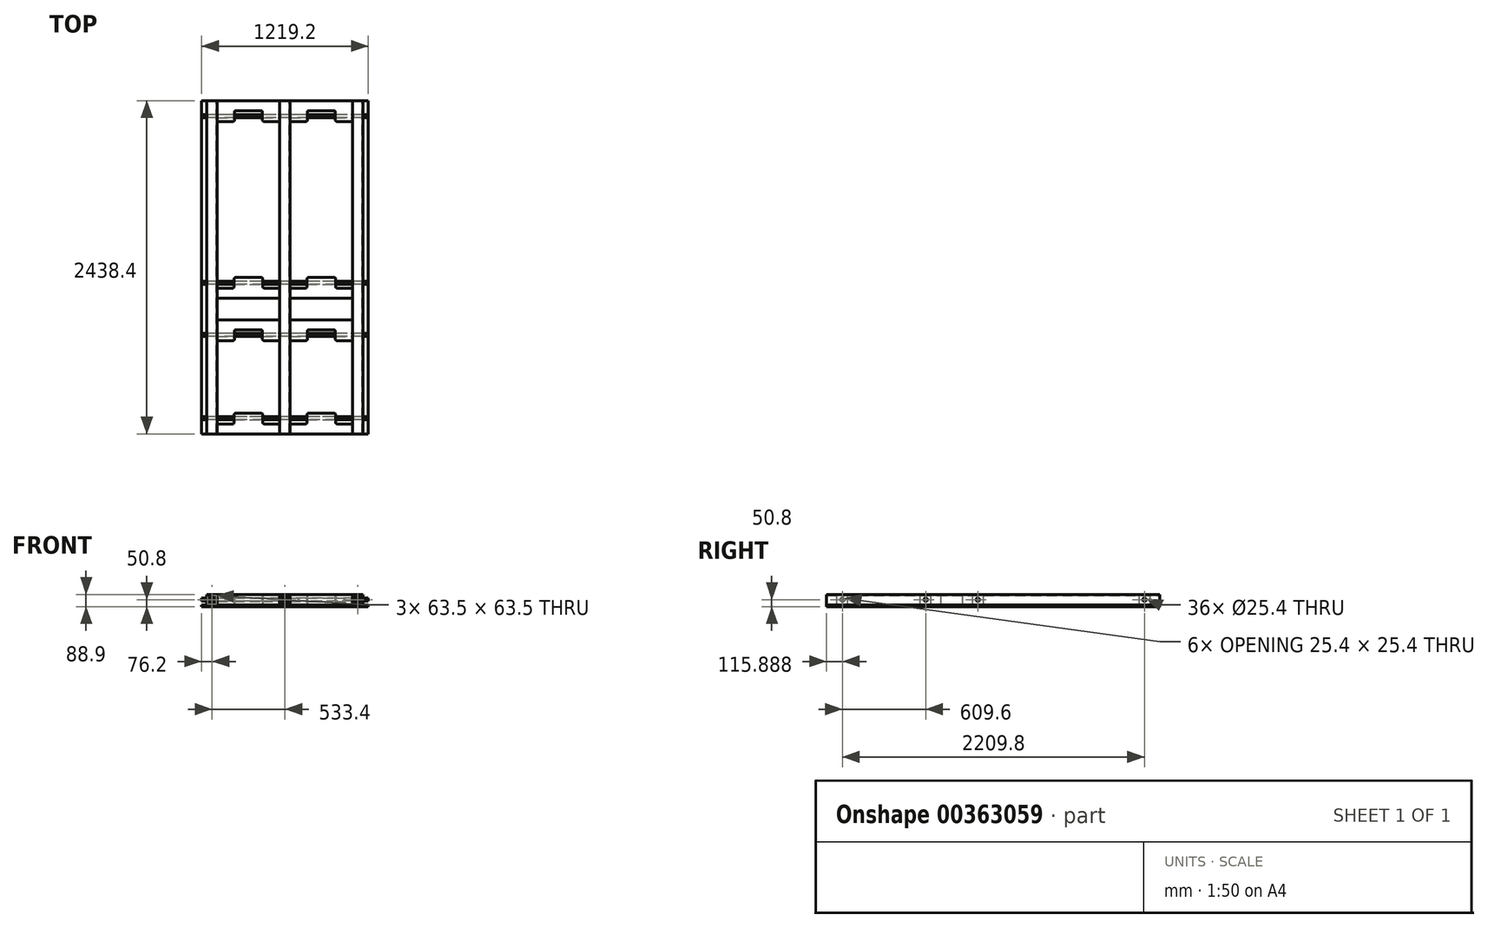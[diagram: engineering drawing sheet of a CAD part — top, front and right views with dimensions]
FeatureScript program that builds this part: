
annotation { "Feature Type Name" : "Feature", "Feature Type Description" : "" }
export const myFeature = defineFeature(function(context is Context, id is Id, definition is map)
    precondition{}
    {
        {
            var Q0;
            Q0=qCreatedBy(makeId("Top.planeOp"),FACE);
            var sketch = newSketch(context, id + "F0", { "sketchPlane" : qUnion([Q0])});
            skLineSegment(sketch, "E0.bottom", {"start": v(-609.6, 1219.2) * mm, "end": v(609.6, 1219.2) * mm});
            skLineSegment(sketch, "E0.top", {"start": v(-609.6, -1219.2) * mm, "end": v(609.6, -1219.2) * mm});
            skLineSegment(sketch, "E0.left", {"start": v(-609.6, 1219.2) * mm, "end": v(-609.6, -1219.2) * mm});
            skLineSegment(sketch, "E0.right", {"start": v(609.6, 1219.2) * mm, "end": v(609.6, -1219.2) * mm});
            skPoint(sketch, "E0.middle", {"position": v(0, 0) * mm});
            skSolve(sketch);
        }
        {
            var Q0;
            Q0 = qSketchRegion(id + "F0", true);
            extrude(context, id + "F1", {"entities" : qUnion([Q0]), "depth" : 12.7 * mm});
        }
        {
            var Q0;
            Q0=qCreatedBy(makeId("Front.planeOp"),FACE);
            var sketch = newSketch(context, id + "F2", { "sketchPlane" : qUnion([Q0])});
            skLineSegment(sketch, "E1.bottom", {"start": v(38.1, 88.9) * mm, "end": v(-38.1, 88.9) * mm});
            skLineSegment(sketch, "E1.top", {"start": v(38.1, 12.7) * mm, "end": v(-38.1, 12.7) * mm});
            skLineSegment(sketch, "E1.left", {"start": v(38.1, 88.9) * mm, "end": v(38.1, 12.7) * mm});
            skLineSegment(sketch, "E1.right", {"start": v(-38.1, 88.9) * mm, "end": v(-38.1, 12.7) * mm});
            skPoint(sketch, "E1.middle", {"position": v(0, 50.8) * mm});
            skLineSegment(sketch, "E2.bottom", {"start": v(31.75, 82.55) * mm, "end": v(-31.75, 82.55) * mm});
            skLineSegment(sketch, "E2.top", {"start": v(31.75, 19.05) * mm, "end": v(-31.75, 19.05) * mm});
            skLineSegment(sketch, "E2.left", {"start": v(31.75, 82.55) * mm, "end": v(31.75, 19.05) * mm});
            skLineSegment(sketch, "E2.right", {"start": v(-31.75, 82.55) * mm, "end": v(-31.75, 19.05) * mm});
            skLineSegment(sketch, "E3.bottom", {"start": v(-495.3, 88.9) * mm, "end": v(-571.5, 88.9) * mm});
            skLineSegment(sketch, "E3.top", {"start": v(-495.3, 12.7) * mm, "end": v(-571.5, 12.7) * mm});
            skLineSegment(sketch, "E3.left", {"start": v(-495.3, 88.9) * mm, "end": v(-495.3, 12.7) * mm});
            skLineSegment(sketch, "E3.right", {"start": v(-571.5, 88.9) * mm, "end": v(-571.5, 12.7) * mm});
            skPoint(sketch, "E3.middle", {"position": v(-533.4, 50.8) * mm});
            skLineSegment(sketch, "E4.bottom", {"start": v(571.5, 88.9) * mm, "end": v(495.3, 88.9) * mm});
            skLineSegment(sketch, "E4.top", {"start": v(571.5, 12.7) * mm, "end": v(495.3, 12.7) * mm});
            skLineSegment(sketch, "E4.left", {"start": v(571.5, 88.9) * mm, "end": v(571.5, 12.7) * mm});
            skLineSegment(sketch, "E4.right", {"start": v(495.3, 88.9) * mm, "end": v(495.3, 12.7) * mm});
            skPoint(sketch, "E4.middle", {"position": v(533.4, 50.8) * mm});
            skLineSegment(sketch, "E5.bottom", {"start": v(-565.15, 82.55) * mm, "end": v(-501.65, 82.55) * mm});
            skLineSegment(sketch, "E5.top", {"start": v(-565.15, 19.05) * mm, "end": v(-501.65, 19.05) * mm});
            skLineSegment(sketch, "E5.left", {"start": v(-565.15, 82.55) * mm, "end": v(-565.15, 19.05) * mm});
            skLineSegment(sketch, "E5.right", {"start": v(-501.65, 82.55) * mm, "end": v(-501.65, 19.05) * mm});
            skLineSegment(sketch, "E6.bottom", {"start": v(501.65, 82.55) * mm, "end": v(565.15, 82.55) * mm});
            skLineSegment(sketch, "E6.top", {"start": v(501.65, 19.05) * mm, "end": v(565.15, 19.05) * mm});
            skLineSegment(sketch, "E6.left", {"start": v(501.65, 82.55) * mm, "end": v(501.65, 19.05) * mm});
            skLineSegment(sketch, "E6.right", {"start": v(565.15, 82.55) * mm, "end": v(565.15, 19.05) * mm});
            skSolve(sketch);
        }
        {
            var Q0;
            Q0 = qSketchRegion(id + "F2", true);
            extrude(context, id + "F3", {"entities" : qUnion([Q0]), "endBound" : BoundingType.SYMMETRIC, "depth" : 2438.4 * mm});
        }
        {
            var Q0;
            Q0=makeQuery(id+"F1.opExtrude","CAP_FACE",FACE,{"disambiguationData":[OSD([sQuery(id+"F0.wireOp",EDGE,"E0.bottom"),sQuery(id+"F0.wireOp",EDGE,"E0.top"),sQuery(id+"F0.wireOp",EDGE,"E0.left"),sQuery(id+"F0.wireOp",EDGE,"E0.right")])],"isStart":false});
            var sketch = newSketch(context, id + "F4", { "sketchPlane" : qUnion([Q0])});
            skLineSegment(sketch, "E7", {"start": v(-495.3, 1219.2) * mm, "end": v(-495.3, 1066.8) * mm});
            skLineSegment(sketch, "E8", {"start": v(-495.3, 1066.8) * mm, "end": v(-368.3, 1066.8) * mm});
            skLineSegment(sketch, "E9", {"start": v(-368.3, 1066.8) * mm, "end": v(-368.3, 1146.18) * mm});
            skLineSegment(sketch, "E10", {"start": v(-368.3, 1146.17) * mm, "end": v(-165.1, 1146.17) * mm});
            skLineSegment(sketch, "E11", {"start": v(-165.1, 1146.18) * mm, "end": v(-165.1, 1066.8) * mm});
            skLineSegment(sketch, "E12", {"start": v(-165.1, 1066.8) * mm, "end": v(-38.1, 1066.8) * mm});
            skLineSegment(sketch, "E13", {"start": v(-38.1, 1066.8) * mm, "end": v(-38.1, 1219.2) * mm});
            skLineSegment(sketch, "E14", {"start": v(-38.1, 1219.2) * mm, "end": v(-495.3, 1219.2) * mm});
            skLineSegment(sketch, "E15", {"start": v(-495.3, -152.4) * mm, "end": v(-371.48, -152.4) * mm});
            skLineSegment(sketch, "E16", {"start": v(-371.48, -152.4) * mm, "end": v(-371.48, -73.03) * mm});
            skLineSegment(sketch, "E17", {"start": v(-371.48, -73.03) * mm, "end": v(-161.93, -73.03) * mm});
            skLineSegment(sketch, "E18", {"start": v(-161.93, -73.02) * mm, "end": v(-161.93, -152.4) * mm});
            skLineSegment(sketch, "E19", {"start": v(-161.93, -152.4) * mm, "end": v(-38.1, -152.4) * mm});
            skLineSegment(sketch, "E20", {"start": v(-38.1, -152.4) * mm, "end": v(-38.1, -536.57) * mm});
            skLineSegment(sketch, "E21", {"start": v(-38.1, -536.57) * mm, "end": v(-165.1, -536.57) * mm});
            skLineSegment(sketch, "E22", {"start": v(-165.1, -536.57) * mm, "end": v(-165.1, -457.2) * mm});
            skLineSegment(sketch, "E23", {"start": v(-165.1, -457.2) * mm, "end": v(-368.3, -457.2) * mm});
            skLineSegment(sketch, "E24", {"start": v(-368.3, -457.2) * mm, "end": v(-368.3, -536.57) * mm});
            skLineSegment(sketch, "E25", {"start": v(-368.3, -536.57) * mm, "end": v(-495.3, -536.57) * mm});
            skLineSegment(sketch, "E26", {"start": v(-495.3, -536.57) * mm, "end": v(-495.3, -152.4) * mm});
            skLineSegment(sketch, "E27", {"start": v(-495.3, -1219.2) * mm, "end": v(-38.1, -1219.2) * mm});
            skLineSegment(sketch, "E28", {"start": v(-38.1, -1219.2) * mm, "end": v(-38.1, -1146.18) * mm});
            skLineSegment(sketch, "E29", {"start": v(-38.1, -1146.18) * mm, "end": v(-161.93, -1146.18) * mm});
            skLineSegment(sketch, "E30", {"start": v(-161.93, -1146.18) * mm, "end": v(-161.93, -1066.8) * mm});
            skLineSegment(sketch, "E31", {"start": v(-161.93, -1066.8) * mm, "end": v(-371.48, -1066.8) * mm});
            skLineSegment(sketch, "E32", {"start": v(-371.48, -1066.8) * mm, "end": v(-371.48, -1146.18) * mm});
            skLineSegment(sketch, "E33", {"start": v(-371.48, -1146.18) * mm, "end": v(-495.3, -1146.18) * mm});
            skLineSegment(sketch, "E34", {"start": v(-495.3, -1146.18) * mm, "end": v(-495.3, -1219.2) * mm});
            skLineSegment(sketch, "E35", {"start": v(-266.7, -1066.8) * mm, "end": v(-266.7, -457.2) * mm, "construction": true});
            skLineSegment(sketch, "E36", {"start": v(-266.7, -73.03) * mm, "end": v(-266.7, 1146.17) * mm, "construction": true});
            skLineSegment(sketch, "E37", {"start": v(-368.3, 1106.49) * mm, "end": v(-165.1, 1106.49) * mm, "construction": true});
            skLineSegment(sketch, "E38", {"start": v(-371.48, -112.71) * mm, "end": v(-161.93, -112.71) * mm, "construction": true});
            skLineSegment(sketch, "E39", {"start": v(-368.3, -496.89) * mm, "end": v(-165.1, -496.89) * mm, "construction": true});
            skLineSegment(sketch, "E40", {"start": v(-371.48, -1106.49) * mm, "end": v(-161.93, -1106.49) * mm, "construction": true});
            skLineSegment(sketch, "E41", {"start": v(0, 0) * mm, "end": v(0, 1271.87) * mm, "construction": true});
            skLineSegment(sketch, "E42.MirrorCS", {"start": v(371.48, -152.4) * mm, "end": v(371.48, -73.02) * mm});
            skLineSegment(sketch, "E43.MirrorCS", {"start": v(161.93, -1146.18) * mm, "end": v(161.93, -1066.8) * mm});
            skLineSegment(sketch, "E44.MirrorCS", {"start": v(165.1, 1146.18) * mm, "end": v(165.1, 1066.8) * mm});
            skLineSegment(sketch, "E45.MirrorCS", {"start": v(165.1, -536.57) * mm, "end": v(165.1, -457.2) * mm});
            skLineSegment(sketch, "E46.MirrorCS", {"start": v(161.93, -73.02) * mm, "end": v(161.93, -152.4) * mm});
            skLineSegment(sketch, "E47.MirrorCS", {"start": v(368.3, -457.2) * mm, "end": v(368.3, -536.57) * mm});
            skLineSegment(sketch, "E48.MirrorCS", {"start": v(368.3, 1066.8) * mm, "end": v(368.3, 1146.18) * mm});
            skLineSegment(sketch, "E49.MirrorCS", {"start": v(371.48, -1066.8) * mm, "end": v(371.48, -1146.18) * mm});
            skLineSegment(sketch, "E50.MirrorCS", {"start": v(371.48, -1146.18) * mm, "end": v(495.3, -1146.18) * mm});
            skLineSegment(sketch, "E51.MirrorCS", {"start": v(495.3, -536.57) * mm, "end": v(495.3, -152.4) * mm});
            skLineSegment(sketch, "E52.MirrorCS", {"start": v(371.48, -112.71) * mm, "end": v(161.93, -112.71) * mm, "construction": true});
            skLineSegment(sketch, "E53.MirrorCS", {"start": v(368.3, 1146.18) * mm, "end": v(165.1, 1146.18) * mm});
            skLineSegment(sketch, "E54.MirrorCS", {"start": v(368.3, -536.57) * mm, "end": v(495.3, -536.57) * mm});
            skLineSegment(sketch, "E55.MirrorCS", {"start": v(371.48, -1106.49) * mm, "end": v(161.93, -1106.49) * mm, "construction": true});
            skLineSegment(sketch, "E56.MirrorCS", {"start": v(266.7, -1066.8) * mm, "end": v(266.7, -457.2) * mm, "construction": true});
            skLineSegment(sketch, "E57.MirrorCS", {"start": v(38.1, -1146.18) * mm, "end": v(161.93, -1146.18) * mm});
            skLineSegment(sketch, "E58.MirrorCS", {"start": v(495.3, -1219.2) * mm, "end": v(38.1, -1219.2) * mm});
            skLineSegment(sketch, "E59.MirrorCS", {"start": v(495.3, -1146.18) * mm, "end": v(495.3, -1219.2) * mm});
            skLineSegment(sketch, "E60.MirrorCS", {"start": v(368.3, -496.89) * mm, "end": v(165.1, -496.89) * mm, "construction": true});
            skLineSegment(sketch, "E61.MirrorCS", {"start": v(266.7, -73.03) * mm, "end": v(266.7, 1146.17) * mm, "construction": true});
            skLineSegment(sketch, "E62.MirrorCS", {"start": v(368.3, 1106.49) * mm, "end": v(165.1, 1106.49) * mm, "construction": true});
            skLineSegment(sketch, "E63.MirrorCS", {"start": v(161.93, -1066.8) * mm, "end": v(371.48, -1066.8) * mm});
            skLineSegment(sketch, "E64.MirrorCS", {"start": v(165.1, 1066.8) * mm, "end": v(38.1, 1066.8) * mm});
            skLineSegment(sketch, "E65.MirrorCS", {"start": v(495.3, -152.4) * mm, "end": v(371.48, -152.4) * mm});
            skLineSegment(sketch, "E66.MirrorCS", {"start": v(38.1, 1219.2) * mm, "end": v(495.3, 1219.2) * mm});
            skLineSegment(sketch, "E67.MirrorCS", {"start": v(38.1, -152.4) * mm, "end": v(38.1, -536.57) * mm});
            skLineSegment(sketch, "E68.MirrorCS", {"start": v(165.1, -457.2) * mm, "end": v(368.3, -457.2) * mm});
            skLineSegment(sketch, "E69.MirrorCS", {"start": v(161.93, -152.4) * mm, "end": v(38.1, -152.4) * mm});
            skLineSegment(sketch, "E70.MirrorCS", {"start": v(38.1, -536.57) * mm, "end": v(165.1, -536.57) * mm});
            skLineSegment(sketch, "E71.MirrorCS", {"start": v(371.48, -73.03) * mm, "end": v(161.93, -73.03) * mm});
            skLineSegment(sketch, "E72.MirrorCS", {"start": v(38.1, -1219.2) * mm, "end": v(38.1, -1146.18) * mm});
            skLineSegment(sketch, "E73.MirrorCS", {"start": v(38.1, 1066.8) * mm, "end": v(38.1, 1219.2) * mm});
            skLineSegment(sketch, "E74.MirrorCS", {"start": v(495.3, 1066.8) * mm, "end": v(368.3, 1066.8) * mm});
            skLineSegment(sketch, "E75.MirrorCS", {"start": v(495.3, 1219.2) * mm, "end": v(495.3, 1066.8) * mm});
            skLineSegment(sketch, "E76", {"start": v(-495.3, -384.17) * mm, "end": v(-38.1, -384.17) * mm});
            skLineSegment(sketch, "E77", {"start": v(-38.1, -384.17) * mm, "end": v(-38.1, -225.43) * mm});
            skLineSegment(sketch, "E78", {"start": v(-38.1, -225.43) * mm, "end": v(-495.3, -225.43) * mm});
            skLineSegment(sketch, "E79.MirrorCS", {"start": v(38.1, -225.43) * mm, "end": v(495.3, -225.42) * mm});
            skLineSegment(sketch, "E80.MirrorCS", {"start": v(495.3, -384.17) * mm, "end": v(38.1, -384.17) * mm});
            skSolve(sketch);
        }
        {
            var Q0;
            Q0=makeQuery(id+"F4.imprint","IMPRINT",FACE,{"disambiguationData":[TD([[makeQuery(id+"F4.imprint","IMPRINT",EDGE,{"derivedFrom":sQuery(id+"F4.wireOp",EDGE,"E7")}),1.0]])]});
            var Q1;
            Q1=makeQuery(id+"F4.imprint","IMPRINT",FACE,{"disambiguationData":[TD([[makeQuery(id+"F4.imprint","IMPRINT",EDGE,{"derivedFrom":sQuery(id+"F4.wireOp",EDGE,"E27")}),1.0]])]});
            var Q2;
            Q2=makeQuery(id+"F4.imprint","IMPRINT",FACE,{"disambiguationData":[TD([[makeQuery(id+"F4.imprint","IMPRINT",EDGE,{"derivedFrom":sQuery(id+"F4.wireOp",EDGE,"E42.MirrorCS")}),1.0]])]});
            var Q3;
            Q3=makeQuery(id+"F4.imprint","IMPRINT",FACE,{"disambiguationData":[TD([[makeQuery(id+"F4.imprint","IMPRINT",EDGE,{"derivedFrom":sQuery(id+"F4.wireOp",EDGE,"E43.MirrorCS")}),-1.0]])]});
            var Q4;
            Q4=makeQuery(id+"F4.imprint","IMPRINT",FACE,{"disambiguationData":[TD([[makeQuery(id+"F4.imprint","IMPRINT",EDGE,{"derivedFrom":sQuery(id+"F4.wireOp",EDGE,"E44.MirrorCS")}),-1.0]])]});
            var Q5;
            {var subQ1=sQuery(id+"F4.wireOp",EDGE,"E15");Q5=makeQuery(id+"F4.imprint","IMPRINT",FACE,{"disambiguationData":[TD([[makeQuery(id+"F4.imprint","IMPRINT",EDGE,{"derivedFrom":subQ1}),-1.0]])]});}
            var Q6;
            {var subQ0=sQuery(id+"F4.wireOp",EDGE,"E21");Q6=makeQuery(id+"F4.imprint","IMPRINT",FACE,{"disambiguationData":[TD([[makeQuery(id+"F4.imprint","IMPRINT",EDGE,{"derivedFrom":subQ0}),-1.0]])]});}
            var Q7;
            Q7=makeQuery(id+"F4.imprint","IMPRINT",FACE,{"disambiguationData":[TD([[makeQuery(id+"F4.imprint","IMPRINT",EDGE,{"derivedFrom":sQuery(id+"F4.wireOp",EDGE,"E45.MirrorCS")}),1.0]])]});
            extrude(context, id + "F5", {"entities" : qUnion([Q0, Q1, Q2, Q3, Q4, Q5, Q6, Q7]), "depth" : 76.2 * mm});
        }
        {
            var Q0;
            Q0=qCreatedBy(makeId("Right.planeOp"),FACE);
            var sketch = newSketch(context, id + "F6", { "sketchPlane" : qUnion([Q0])});
            skCircle(sketch, "E81", {"center": v(-1103.31, 50.8) * mm, "radius": 12.7 * mm});
            skCircle(sketch, "E82", {"center": v(-493.71, 50.8) * mm, "radius": 12.7 * mm});
            skCircle(sketch, "E83", {"center": v(-112.71, 50.8) * mm, "radius": 12.7 * mm});
            skCircle(sketch, "E84", {"center": v(1106.49, 50.8) * mm, "radius": 12.7 * mm});
            skSolve(sketch);
        }
        {
            var Q0;
            Q0 = qSketchRegion(id + "F6", true);
            extrude(context, id + "F7", {"entities" : qUnion([Q0]), "operationType" : NewBodyOperationType.REMOVE, "endBound" : BoundingType.SYMMETRIC, "oppositeDirection" : true, "depth" : 1219.2 * mm});
        }
        {
            var Q0;
            Q0=qCreatedBy(makeId("Right.planeOp"),FACE);
            var sketch = newSketch(context, id + "F8", { "sketchPlane" : qUnion([Q0])});
            skCircle(sketch, "E85", {"center": v(-1103.31, 50.8) * mm, "radius": 11.11 * mm});
            skCircle(sketch, "E86", {"center": v(-493.71, 50.8) * mm, "radius": 11.11 * mm});
            skCircle(sketch, "E87", {"center": v(-112.71, 50.8) * mm, "radius": 11.11 * mm});
            skCircle(sketch, "E88", {"center": v(1106.49, 50.8) * mm, "radius": 11.11 * mm});
            skSolve(sketch);
        }
        {
            var Q0;
            Q0 = qSketchRegion(id + "F8", true);
            extrude(context, id + "F9", {"entities" : qUnion([Q0]), "endBound" : BoundingType.SYMMETRIC, "depth" : 1219.2 * mm});
        }
        {
            var Q0;
            Q0=makeQuery(id+"F5.opExtrude","SWEPT_EDGE",EDGE,{"disambiguationData":[OSD([sQuery(id+"F4.wireOp",EDGE,"E23"),sQuery(id+"F4.wireOp",EDGE,"E24")])]});
            var Q1;
            Q1=makeQuery(id+"F5.opExtrude","SWEPT_EDGE",EDGE,{"disambiguationData":[OSD([sQuery(id+"F4.wireOp",EDGE,"E45.MirrorCS"),sQuery(id+"F4.wireOp",EDGE,"E68.MirrorCS")])]});
            var Q2;
            Q2=makeQuery(id+"F5.opExtrude","SWEPT_EDGE",EDGE,{"disambiguationData":[OSD([sQuery(id+"F4.wireOp",EDGE,"E47.MirrorCS"),sQuery(id+"F4.wireOp",EDGE,"E68.MirrorCS")])]});
            var Q3;
            Q3=makeQuery(id+"F5.opExtrude","SWEPT_EDGE",EDGE,{"disambiguationData":[OSD([sQuery(id+"F4.wireOp",EDGE,"E22"),sQuery(id+"F4.wireOp",EDGE,"E23")])]});
            var Q4;
            Q4=makeQuery(id+"F5.opExtrude","SWEPT_EDGE",EDGE,{"disambiguationData":[OSD([sQuery(id+"F4.wireOp",EDGE,"E9"),sQuery(id+"F4.wireOp",EDGE,"E10")])]});
            var Q5;
            Q5=makeQuery(id+"F5.opExtrude","SWEPT_EDGE",EDGE,{"disambiguationData":[OSD([sQuery(id+"F4.wireOp",EDGE,"E44.MirrorCS"),sQuery(id+"F4.wireOp",EDGE,"E53.MirrorCS")])]});
            var Q6;
            Q6=makeQuery(id+"F5.opExtrude","SWEPT_EDGE",EDGE,{"disambiguationData":[OSD([sQuery(id+"F4.wireOp",EDGE,"E48.MirrorCS"),sQuery(id+"F4.wireOp",EDGE,"E53.MirrorCS")])]});
            var Q7;
            Q7=makeQuery(id+"F5.opExtrude","SWEPT_EDGE",EDGE,{"disambiguationData":[OSD([sQuery(id+"F4.wireOp",EDGE,"E10"),sQuery(id+"F4.wireOp",EDGE,"E11")])]});
            fillet(context, id + "F10", {"entities" : qUnion([Q0, Q1, Q2, Q3, Q4, Q5, Q6, Q7]), "radius" : 9.52 * mm, "tangentPropagation" : true, "allowEdgeOverflow" : false});
        }
        {
            var Q0;
            Q0=makeQuery(id+"F5.opExtrude","SWEPT_EDGE",EDGE,{"disambiguationData":[OSD([sQuery(id+"F4.wireOp",EDGE,"E16"),sQuery(id+"F4.wireOp",EDGE,"E17")])]});
            var Q1;
            Q1=makeQuery(id+"F5.opExtrude","SWEPT_EDGE",EDGE,{"disambiguationData":[OSD([sQuery(id+"F4.wireOp",EDGE,"E17"),sQuery(id+"F4.wireOp",EDGE,"E18")])]});
            var Q2;
            Q2=makeQuery(id+"F5.opExtrude","SWEPT_EDGE",EDGE,{"disambiguationData":[OSD([sQuery(id+"F4.wireOp",EDGE,"E46.MirrorCS"),sQuery(id+"F4.wireOp",EDGE,"E71.MirrorCS")])]});
            var Q3;
            Q3=makeQuery(id+"F5.opExtrude","SWEPT_EDGE",EDGE,{"disambiguationData":[OSD([sQuery(id+"F4.wireOp",EDGE,"E42.MirrorCS"),sQuery(id+"F4.wireOp",EDGE,"E71.MirrorCS")])]});
            var Q4;
            Q4=makeQuery(id+"F5.opExtrude","SWEPT_EDGE",EDGE,{"disambiguationData":[OSD([sQuery(id+"F4.wireOp",EDGE,"E31"),sQuery(id+"F4.wireOp",EDGE,"E32")])]});
            var Q5;
            Q5=makeQuery(id+"F5.opExtrude","SWEPT_EDGE",EDGE,{"disambiguationData":[OSD([sQuery(id+"F4.wireOp",EDGE,"E30"),sQuery(id+"F4.wireOp",EDGE,"E31")])]});
            var Q6;
            Q6=makeQuery(id+"F5.opExtrude","SWEPT_EDGE",EDGE,{"disambiguationData":[OSD([sQuery(id+"F4.wireOp",EDGE,"E43.MirrorCS"),sQuery(id+"F4.wireOp",EDGE,"E63.MirrorCS")])]});
            var Q7;
            Q7=makeQuery(id+"F5.opExtrude","SWEPT_EDGE",EDGE,{"disambiguationData":[OSD([sQuery(id+"F4.wireOp",EDGE,"E49.MirrorCS"),sQuery(id+"F4.wireOp",EDGE,"E63.MirrorCS")])]});
            fillet(context, id + "F11", {"entities" : qUnion([Q0, Q1, Q2, Q3, Q4, Q5, Q6, Q7]), "radius" : 12.7 * mm, "tangentPropagation" : true, "allowEdgeOverflow" : false});
        }
        {
            var Q0;
            Q0=makeQuery(id+"F5.opExtrude","SWEPT_EDGE",EDGE,{"disambiguationData":[OSD([sQuery(id+"F4.wireOp",EDGE,"E24"),sQuery(id+"F4.wireOp",EDGE,"E25")])]});
            var Q1;
            Q1=makeQuery(id+"F5.opExtrude","SWEPT_EDGE",EDGE,{"disambiguationData":[OSD([sQuery(id+"F4.wireOp",EDGE,"E21"),sQuery(id+"F4.wireOp",EDGE,"E22")])]});
            var Q2;
            Q2=makeQuery(id+"F5.opExtrude","SWEPT_EDGE",EDGE,{"disambiguationData":[OSD([sQuery(id+"F4.wireOp",EDGE,"E8"),sQuery(id+"F4.wireOp",EDGE,"E9")])]});
            var Q3;
            Q3=makeQuery(id+"F5.opExtrude","SWEPT_EDGE",EDGE,{"disambiguationData":[OSD([sQuery(id+"F4.wireOp",EDGE,"E11"),sQuery(id+"F4.wireOp",EDGE,"E12")])]});
            var Q4;
            Q4=makeQuery(id+"F5.opExtrude","SWEPT_EDGE",EDGE,{"disambiguationData":[OSD([sQuery(id+"F4.wireOp",EDGE,"E44.MirrorCS"),sQuery(id+"F4.wireOp",EDGE,"E64.MirrorCS")])]});
            var Q5;
            Q5=makeQuery(id+"F5.opExtrude","SWEPT_EDGE",EDGE,{"disambiguationData":[OSD([sQuery(id+"F4.wireOp",EDGE,"E48.MirrorCS"),sQuery(id+"F4.wireOp",EDGE,"E74.MirrorCS")])]});
            var Q6;
            Q6=makeQuery(id+"F5.opExtrude","SWEPT_EDGE",EDGE,{"disambiguationData":[OSD([sQuery(id+"F4.wireOp",EDGE,"E45.MirrorCS"),sQuery(id+"F4.wireOp",EDGE,"E70.MirrorCS")])]});
            var Q7;
            Q7=makeQuery(id+"F5.opExtrude","SWEPT_EDGE",EDGE,{"disambiguationData":[OSD([sQuery(id+"F4.wireOp",EDGE,"E47.MirrorCS"),sQuery(id+"F4.wireOp",EDGE,"E54.MirrorCS")])]});
            fillet(context, id + "F12", {"entities" : qUnion([Q0, Q1, Q2, Q3, Q4, Q5, Q6, Q7]), "radius" : 12.7 * mm, "tangentPropagation" : true, "allowEdgeOverflow" : false});
        }
        {
            var Q0;
            Q0=makeQuery(id+"F5.opExtrude","SWEPT_EDGE",EDGE,{"disambiguationData":[OSD([sQuery(id+"F4.wireOp",EDGE,"E42.MirrorCS"),sQuery(id+"F4.wireOp",EDGE,"E65.MirrorCS")])]});
            var Q1;
            Q1=makeQuery(id+"F5.opExtrude","SWEPT_EDGE",EDGE,{"disambiguationData":[OSD([sQuery(id+"F4.wireOp",EDGE,"E46.MirrorCS"),sQuery(id+"F4.wireOp",EDGE,"E69.MirrorCS")])]});
            var Q2;
            Q2=makeQuery(id+"F5.opExtrude","SWEPT_EDGE",EDGE,{"disambiguationData":[OSD([sQuery(id+"F4.wireOp",EDGE,"E15"),sQuery(id+"F4.wireOp",EDGE,"E16")])]});
            var Q3;
            Q3=makeQuery(id+"F5.opExtrude","SWEPT_EDGE",EDGE,{"disambiguationData":[OSD([sQuery(id+"F4.wireOp",EDGE,"E18"),sQuery(id+"F4.wireOp",EDGE,"E19")])]});
            var Q4;
            Q4=makeQuery(id+"F5.opExtrude","SWEPT_EDGE",EDGE,{"disambiguationData":[OSD([sQuery(id+"F4.wireOp",EDGE,"E32"),sQuery(id+"F4.wireOp",EDGE,"E33")])]});
            var Q5;
            Q5=makeQuery(id+"F5.opExtrude","SWEPT_EDGE",EDGE,{"disambiguationData":[OSD([sQuery(id+"F4.wireOp",EDGE,"E29"),sQuery(id+"F4.wireOp",EDGE,"E30")])]});
            var Q6;
            Q6=makeQuery(id+"F5.opExtrude","SWEPT_EDGE",EDGE,{"disambiguationData":[OSD([sQuery(id+"F4.wireOp",EDGE,"E43.MirrorCS"),sQuery(id+"F4.wireOp",EDGE,"E57.MirrorCS")])]});
            var Q7;
            Q7=makeQuery(id+"F5.opExtrude","SWEPT_EDGE",EDGE,{"disambiguationData":[OSD([sQuery(id+"F4.wireOp",EDGE,"E49.MirrorCS"),sQuery(id+"F4.wireOp",EDGE,"E50.MirrorCS")])]});
            fillet(context, id + "F13", {"entities" : qUnion([Q0, Q1, Q2, Q3, Q4, Q5, Q6, Q7]), "radius" : 9.52 * mm, "tangentPropagation" : true, "allowEdgeOverflow" : false});
        }
        {
            var Q0;
            Q0=makeQuery(id+"F3.opExtrude","SWEPT_FACE",FACE,{"disambiguationData":[OSD([sQuery(id+"F2.wireOp",EDGE,"E3.left")])]});
            cPlane(context, id + "F14", {"entities" : qUnion([Q0]), "cplaneType" : CPlaneType.OFFSET, "offset" : 228.6 * mm, "width" : 152.4 * mm, "height" : 152.4 * mm});
        }
    });
